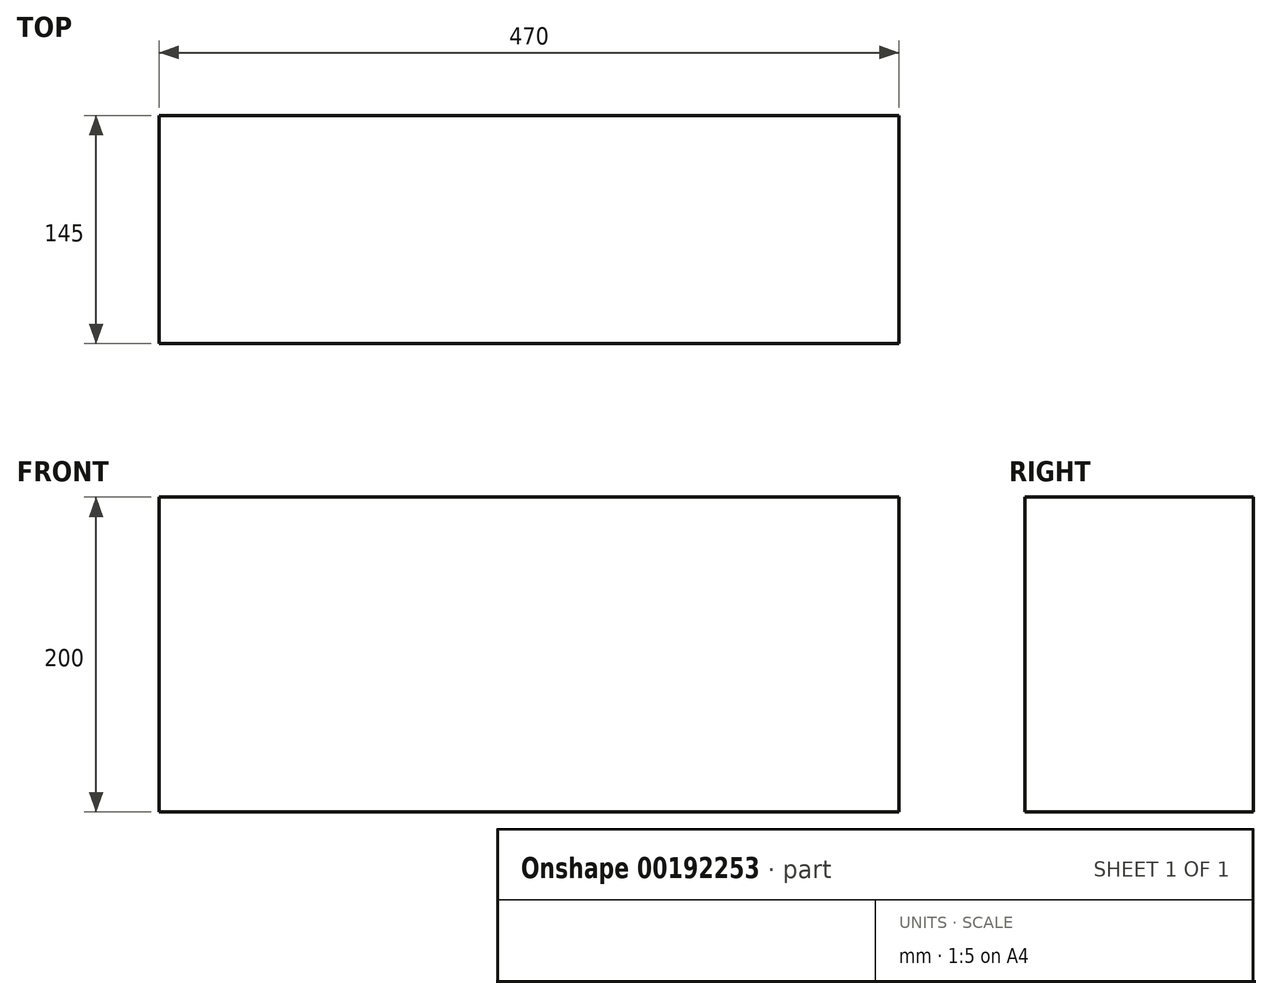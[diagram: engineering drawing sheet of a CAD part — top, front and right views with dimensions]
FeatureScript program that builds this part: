
annotation { "Feature Type Name" : "Feature", "Feature Type Description" : "" }
export const myFeature = defineFeature(function(context is Context, id is Id, definition is map)
    precondition{}
    {
        {
            var Q0;
            Q0=qCreatedBy(makeId("Front.planeOp"),FACE);
            var sketch = newSketch(context, id + "F0", { "sketchPlane" : qUnion([Q0])});
            skLineSegment(sketch, "E0.bottom", {"start": v(235, -100) * mm, "end": v(-235, -100) * mm});
            skLineSegment(sketch, "E0.top", {"start": v(235, 100) * mm, "end": v(-235, 100) * mm});
            skLineSegment(sketch, "E0.left", {"start": v(235, -100) * mm, "end": v(235, 100) * mm});
            skLineSegment(sketch, "E0.right", {"start": v(-235, -100) * mm, "end": v(-235, 100) * mm});
            skPoint(sketch, "E0.middle", {"position": v(0, 0) * mm});
            skSolve(sketch);
        }
        {
            var Q0;
            Q0=makeQuery(id+"F0.imprint","IMPRINT",FACE,{"disambiguationData":[TD([[makeQuery(id+"F0.imprint","IMPRINT",EDGE,{"derivedFrom":sQuery(id+"F0.wireOp",EDGE,"E0.bottom")}),-1.0]])]});
            extrude(context, id + "F1", {"entities" : qUnion([Q0]), "depth" : 145 * mm});
        }
    });
